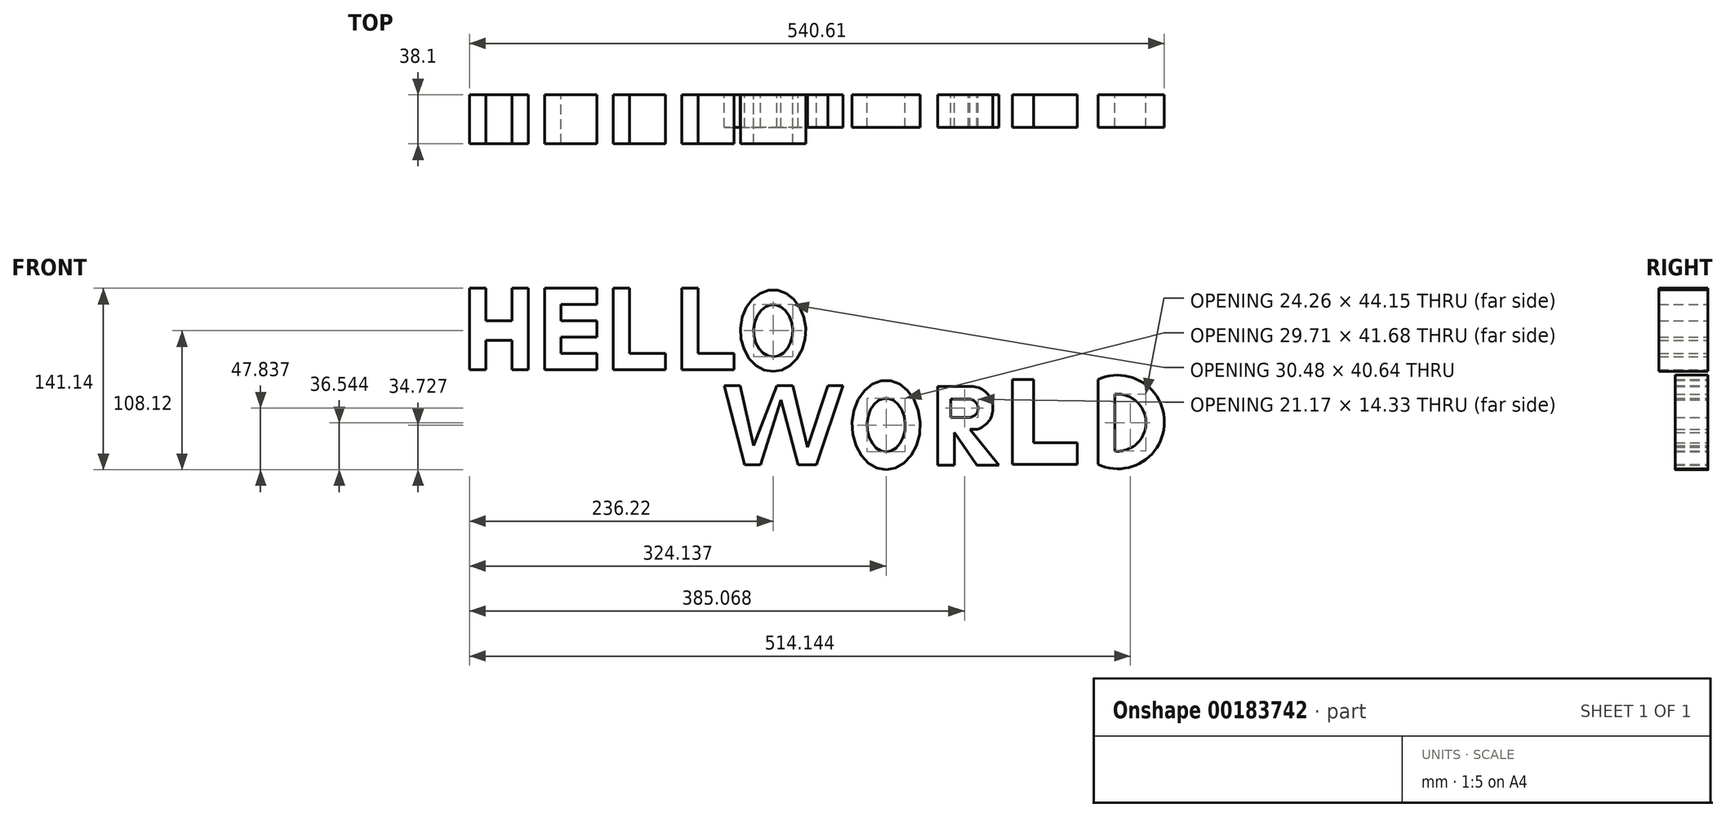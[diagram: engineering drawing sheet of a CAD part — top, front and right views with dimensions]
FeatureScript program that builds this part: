
annotation { "Feature Type Name" : "Feature", "Feature Type Description" : "" }
export const myFeature = defineFeature(function(context is Context, id is Id, definition is map)
    precondition{}
    {
        {
            var Q0;
            Q0=qCreatedBy(makeId("Front.planeOp"),FACE);
            var sketch = newSketch(context, id + "F0", { "sketchPlane" : qUnion([Q0])});
            skLineSegment(sketch, "E0", {"start": v(0, 0) * mm, "end": v(0, 33.02) * mm});
            skLineSegment(sketch, "E1", {"start": v(0, 33.02) * mm, "end": v(12.7, 33.02) * mm});
            skLineSegment(sketch, "E2", {"start": v(12.7, 33.02) * mm, "end": v(12.7, 7.62) * mm});
            skLineSegment(sketch, "E3", {"start": v(12.7, 7.62) * mm, "end": v(33.02, 7.62) * mm});
            skLineSegment(sketch, "E4", {"start": v(33.02, 7.62) * mm, "end": v(33.02, 33.02) * mm});
            skLineSegment(sketch, "E5", {"start": v(33.02, 33.02) * mm, "end": v(45.72, 33.02) * mm});
            skLineSegment(sketch, "E6", {"start": v(45.72, 33.02) * mm, "end": v(45.72, -30.48) * mm});
            skLineSegment(sketch, "E7", {"start": v(45.72, -30.48) * mm, "end": v(33.02, -30.48) * mm});
            skLineSegment(sketch, "E8", {"start": v(33.02, -30.48) * mm, "end": v(33.02, -7.62) * mm});
            skLineSegment(sketch, "E9", {"start": v(33.02, -7.62) * mm, "end": v(12.7, -7.62) * mm});
            skLineSegment(sketch, "E10", {"start": v(12.7, -7.62) * mm, "end": v(12.7, -30.48) * mm});
            skLineSegment(sketch, "E11", {"start": v(12.7, -30.48) * mm, "end": v(0, -30.48) * mm});
            skLineSegment(sketch, "E12", {"start": v(0, -30.48) * mm, "end": v(0, 0) * mm});
            skLineSegment(sketch, "E13", {"start": v(58.42, 33.02) * mm, "end": v(99.06, 33.02) * mm});
            skLineSegment(sketch, "E14", {"start": v(99.06, 33.02) * mm, "end": v(99.06, 20.32) * mm});
            skLineSegment(sketch, "E15", {"start": v(99.06, 20.32) * mm, "end": v(71.12, 20.32) * mm});
            skLineSegment(sketch, "E16", {"start": v(71.12, 20.32) * mm, "end": v(71.12, 7.62) * mm});
            skLineSegment(sketch, "E17", {"start": v(71.12, 7.62) * mm, "end": v(99.06, 7.62) * mm});
            skLineSegment(sketch, "E18", {"start": v(99.06, 7.62) * mm, "end": v(99.06, -5.08) * mm});
            skLineSegment(sketch, "E19", {"start": v(99.06, -5.08) * mm, "end": v(71.12, -5.08) * mm});
            skLineSegment(sketch, "E20", {"start": v(71.12, -5.08) * mm, "end": v(71.12, -17.78) * mm});
            skLineSegment(sketch, "E21", {"start": v(71.12, -17.78) * mm, "end": v(99.06, -17.78) * mm});
            skLineSegment(sketch, "E22", {"start": v(99.06, -17.78) * mm, "end": v(99.06, -30.48) * mm});
            skLineSegment(sketch, "E23", {"start": v(99.06, -30.48) * mm, "end": v(58.42, -30.48) * mm});
            skLineSegment(sketch, "E24", {"start": v(58.42, -30.48) * mm, "end": v(58.42, 33.02) * mm});
            skLineSegment(sketch, "E25", {"start": v(111.76, 33.02) * mm, "end": v(111.76, -30.48) * mm});
            skLineSegment(sketch, "E26", {"start": v(111.76, -30.48) * mm, "end": v(152.4, -30.48) * mm});
            skLineSegment(sketch, "E27", {"start": v(152.4, -30.48) * mm, "end": v(152.4, -17.78) * mm});
            skLineSegment(sketch, "E28", {"start": v(152.4, -17.78) * mm, "end": v(124.46, -17.78) * mm});
            skLineSegment(sketch, "E29", {"start": v(124.46, -17.78) * mm, "end": v(124.46, 33.02) * mm});
            skLineSegment(sketch, "E30", {"start": v(124.46, 33.02) * mm, "end": v(111.76, 33.02) * mm});
            skLineSegment(sketch, "E31", {"start": v(165.1, 33.02) * mm, "end": v(165.1, -30.48) * mm});
            skLineSegment(sketch, "E32", {"start": v(165.1, -30.48) * mm, "end": v(205.74, -30.48) * mm});
            skLineSegment(sketch, "E33", {"start": v(205.74, -30.48) * mm, "end": v(205.74, -17.78) * mm});
            skLineSegment(sketch, "E34", {"start": v(205.74, -17.78) * mm, "end": v(177.8, -17.78) * mm});
            skLineSegment(sketch, "E35", {"start": v(177.8, -17.78) * mm, "end": v(177.8, 33.02) * mm});
            skLineSegment(sketch, "E36", {"start": v(177.8, 33.02) * mm, "end": v(165.1, 33.02) * mm});
            skEllipse(sketch, "E37", {"center": v(236.22, 0) * mm, "majorRadius": 20.32 * mm, "minorRadius": 15.24 * mm, "majorAxis": v(0, -1)});
            skEllipse(sketch, "E38", {"center": v(236.22, 0) * mm, "majorRadius": 31.75 * mm, "minorRadius": 25.4 * mm, "majorAxis": v(0, -1)});
            skSolve(sketch);
        }
        {
            var Q0;
            Q0 = qSketchRegion(id + "F0", true);
            extrude(context, id + "F1", {"entities" : qUnion([Q0]), "depth" : 38.1 * mm});
        }
        {
            var Q0;
            Q0=makeQuery(id+"F1.opExtrude","CAP_FACE",FACE,{"disambiguationData":[OSD([sQuery(id+"F0.wireOp",EDGE,"E37"),sQuery(id+"F0.wireOp",EDGE,"E38")])],"isStart":true});
            var sketch = newSketch(context, id + "F2", { "sketchPlane" : qUnion([Q0])});
            skLineSegment(sketch, "E39", {"start": v(-239.18, -42.63) * mm, "end": v(-251.42, -42.63) * mm});
            skLineSegment(sketch, "E40", {"start": v(-251.42, -42.63) * mm, "end": v(-262.95, -90.52) * mm});
            skLineSegment(sketch, "E41", {"start": v(-262.95, -90.52) * mm, "end": v(-278.69, -42.63) * mm});
            skLineSegment(sketch, "E42", {"start": v(-278.69, -42.63) * mm, "end": v(-290.57, -42.63) * mm});
            skLineSegment(sketch, "E43", {"start": v(-290.57, -42.63) * mm, "end": v(-269.95, -104.16) * mm});
            skLineSegment(sketch, "E44", {"start": v(-269.95, -104.16) * mm, "end": v(-255.61, -104.16) * mm});
            skLineSegment(sketch, "E45", {"start": v(-255.61, -104.16) * mm, "end": v(-242.33, -53.81) * mm});
            skLineSegment(sketch, "E46", {"start": v(-242.33, -53.81) * mm, "end": v(-226.6, -104.16) * mm});
            skLineSegment(sketch, "E47", {"start": v(-226.6, -104.16) * mm, "end": v(-214, -104.16) * mm});
            skLineSegment(sketch, "E48", {"start": v(-214, -104.16) * mm, "end": v(-198.28, -42.63) * mm});
            skLineSegment(sketch, "E49", {"start": v(-198.28, -42.63) * mm, "end": v(-210.51, -42.63) * mm});
            skLineSegment(sketch, "E50", {"start": v(-210.51, -42.63) * mm, "end": v(-221, -89.48) * mm});
            skLineSegment(sketch, "E51", {"start": v(-221, -89.48) * mm, "end": v(-239.18, -42.63) * mm});
            skEllipse(sketch, "E52", {"center": v(-324.14, -73.4) * mm, "majorRadius": 20.84 * mm, "minorRadius": 14.85 * mm, "majorAxis": v(0, -1)});
            skEllipse(sketch, "E53", {"center": v(-324.14, -73.4) * mm, "majorRadius": 34.73 * mm, "minorRadius": 26.53 * mm, "majorAxis": v(0, -1)});
            skLineSegment(sketch, "E54", {"start": v(-364.34, -43.33) * mm, "end": v(-364.34, -104.5) * mm});
            skLineSegment(sketch, "E55", {"start": v(-364.34, -104.5) * mm, "end": v(-377.28, -104.5) * mm});
            skLineSegment(sketch, "E56", {"start": v(-377.28, -104.5) * mm, "end": v(-377.28, -79.34) * mm});
            skLineSegment(sketch, "E57", {"start": v(-377.28, -79.34) * mm, "end": v(-394.76, -104.5) * mm});
            skLineSegment(sketch, "E58", {"start": v(-394.76, -104.5) * mm, "end": v(-411.97, -104.5) * mm});
            skLineSegment(sketch, "E59", {"start": v(-411.97, -104.5) * mm, "end": v(-389.2, -76.54) * mm});
            skLineSegment(sketch, "E60", {"start": v(-364.34, -43.33) * mm, "end": v(-390.21, -43.33) * mm});
            skLineSegment(sketch, "E61", {"start": v(-389.2, -76.54) * mm, "end": v(-395.46, -76.54) * mm});
            skArc(sketch, "E62", {"start": v(-390.21, -43.33) * mm, "mid": v(-407.03, -57.7) * mm, "end": v(-395.46, -76.54) * mm});
            skLineSegment(sketch, "E63", {"start": v(-374.48, -53.12) * mm, "end": v(-374.48, -67.45) * mm});
            skLineSegment(sketch, "E64", {"start": v(-374.48, -67.45) * mm, "end": v(-388.12, -67.45) * mm});
            skLineSegment(sketch, "E65", {"start": v(-374.48, -53.12) * mm, "end": v(-388.49, -53.12) * mm});
            skArc(sketch, "E66", {"start": v(-388.49, -53.12) * mm, "mid": v(-395.65, -60.47) * mm, "end": v(-388.12, -67.45) * mm});
            skLineSegment(sketch, "E67", {"start": v(-422.48, -37.9) * mm, "end": v(-422.48, -104.15) * mm});
            skLineSegment(sketch, "E68", {"start": v(-422.48, -104.15) * mm, "end": v(-472.79, -104.15) * mm});
            skLineSegment(sketch, "E69", {"start": v(-472.79, -104.15) * mm, "end": v(-472.79, -87.1) * mm});
            skLineSegment(sketch, "E70", {"start": v(-472.79, -87.1) * mm, "end": v(-438.7, -87.1) * mm});
            skLineSegment(sketch, "E71", {"start": v(-438.7, -87.1) * mm, "end": v(-438.7, -37.9) * mm});
            skLineSegment(sketch, "E72", {"start": v(-438.7, -37.9) * mm, "end": v(-422.48, -37.9) * mm});
            skLineSegment(sketch, "E73", {"start": v(-489.01, -37.9) * mm, "end": v(-489.01, -104.15) * mm});
            skPoint(sketch, "E73.startSnap0", {"position": v(-430.59, -37.9) * mm});
            skArc(sketch, "E74", {"start": v(-489.01, -37.9) * mm, "mid": v(-540.61, -71.02) * mm, "end": v(-489.01, -104.15) * mm});
            skLineSegment(sketch, "E75", {"start": v(-502.02, -49.5) * mm, "end": v(-502.02, -93.65) * mm});
            skArc(sketch, "E76", {"start": v(-502.02, -49.5) * mm, "mid": v(-526.27, -71.58) * mm, "end": v(-502.02, -93.65) * mm});
            skSolve(sketch);
        }
        {
            var Q0;
            Q0 = qSketchRegion(id + "F2", true);
            extrude(context, id + "F3", {"entities" : qUnion([Q0]), "oppositeDirection" : true, "depth" : 25.4 * mm});
        }
    });
